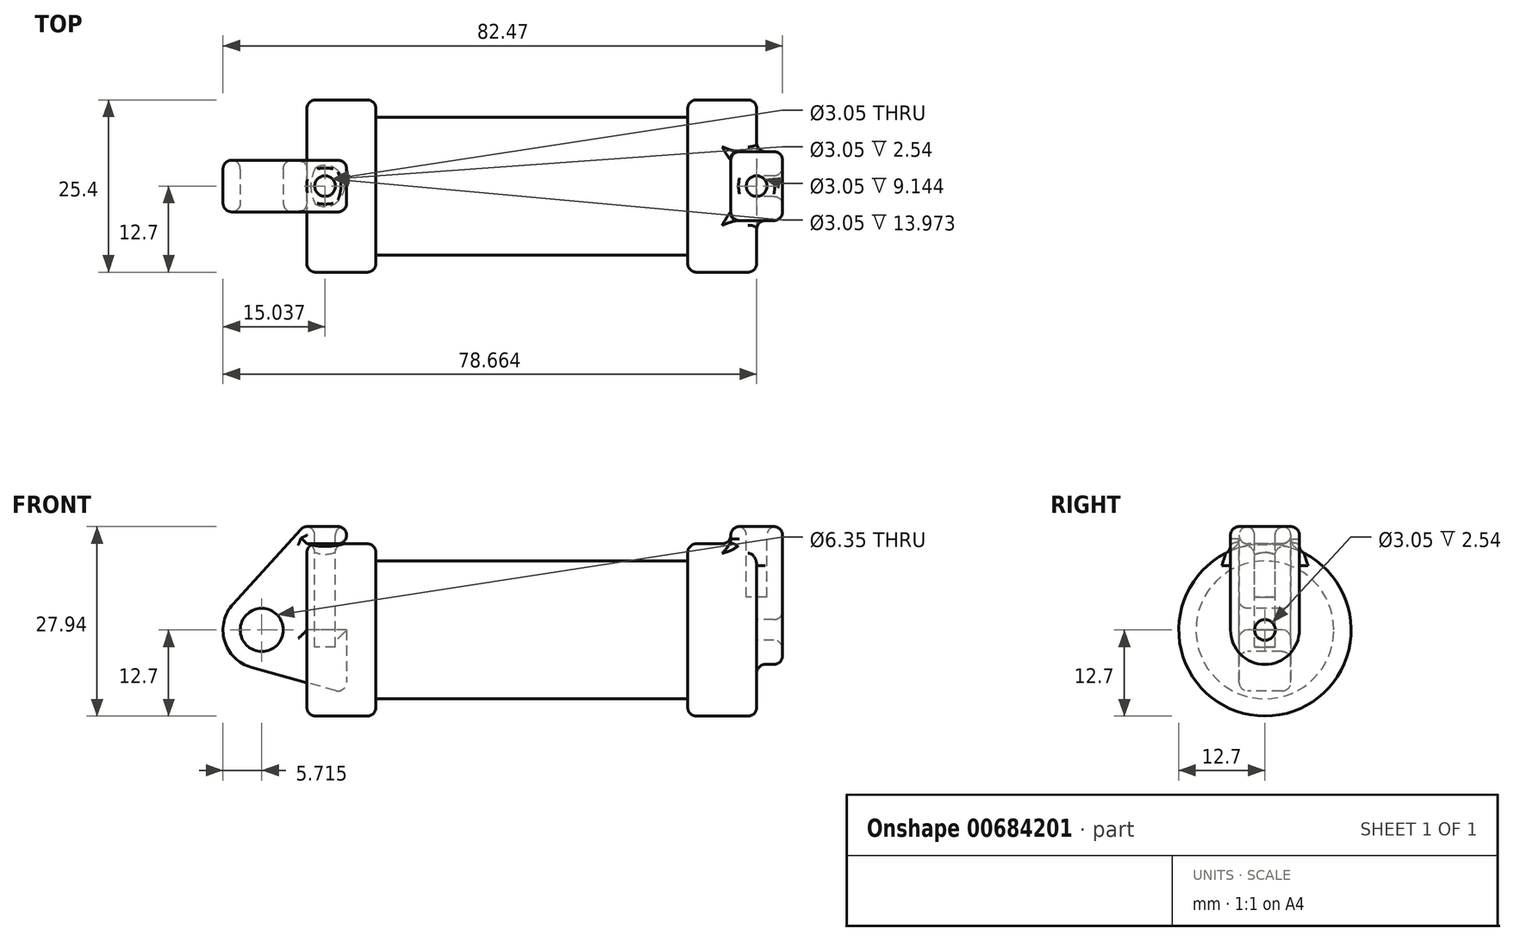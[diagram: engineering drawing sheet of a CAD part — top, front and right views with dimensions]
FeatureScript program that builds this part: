
annotation { "Feature Type Name" : "Feature", "Feature Type Description" : "" }
export const myFeature = defineFeature(function(context is Context, id is Id, definition is map)
    precondition{}
    {
        {
            var Q0;
            Q0=qCreatedBy(makeId("Front.planeOp"),FACE);
            var sketch = newSketch(context, id + "F0", { "sketchPlane" : qUnion([Q0])});
            skLineSegment(sketch, "E0", {"start": v(0, 0) * mm, "end": v(0, 12.7) * mm});
            skLineSegment(sketch, "E1", {"start": v(0, 12.7) * mm, "end": v(10.16, 12.7) * mm});
            skLineSegment(sketch, "E2", {"start": v(10.16, 12.7) * mm, "end": v(10.16, 10.16) * mm});
            skLineSegment(sketch, "E3", {"start": v(10.16, 10.16) * mm, "end": v(56.13, 10.16) * mm});
            skLineSegment(sketch, "E4", {"start": v(56.13, 10.16) * mm, "end": v(56.13, 12.7) * mm});
            skLineSegment(sketch, "E5", {"start": v(56.13, 12.7) * mm, "end": v(66.3, 12.7) * mm});
            skLineSegment(sketch, "E6", {"start": v(66.3, 12.7) * mm, "end": v(66.3, 0) * mm});
            skLineSegment(sketch, "E7", {"start": v(66.3, 0) * mm, "end": v(0, 0) * mm});
            skLineSegment(sketch, "E8", {"start": v(5.84, 15.24) * mm, "end": v(-0.5, 15.24) * mm});
            skLineSegment(sketch, "E9", {"start": v(-0.5, 15.24) * mm, "end": v(-10.88, 3.85) * mm});
            skLineSegment(sketch, "E10", {"start": v(0, 0) * mm, "end": v(-6.65, 0) * mm});
            skCircle(sketch, "E11", {"center": v(-6.65, 0) * mm, "radius": 5.72 * mm});
            skCircle(sketch, "E12", {"center": v(-6.65, 0) * mm, "radius": 3.18 * mm});
            skLineSegment(sketch, "E13", {"start": v(5.84, 15.24) * mm, "end": v(5.84, -9.4) * mm});
            skLineSegment(sketch, "E14", {"start": v(5.84, -9.4) * mm, "end": v(-8.18, -5.5) * mm});
            skSolve(sketch);
        }
        {
            var Q0;
            {var subQ0=sQuery(id+"F0.wireOp",EDGE,"E0");Q0=makeQuery(id+"F0.imprint","IMPRINT",FACE,{"disambiguationData":[TD([[makeQuery(id+"F0.imprint","IMPRINT",EDGE,{"derivedFrom":subQ0}),-1.0]])]});}
            var Q1;
            {var subQ0=sQuery(id+"F0.wireOp",EDGE,"E2");Q1=makeQuery(id+"F0.imprint","IMPRINT",FACE,{"disambiguationData":[TD([[makeQuery(id+"F0.imprint","IMPRINT",EDGE,{"derivedFrom":subQ0}),-1.0]])]});}
            var Q2;
            Q2=sQuery(id+"F0.wireOp",EDGE,"E7");
            var Q3;
            Q3=sQuery(id+"F0.wireOp",EDGE,"E7");
            revolve(context, id + "F1", {"entities" : qUnion([Q0, Q1]), "surfaceEntities" : qUnion([Q2]), "axis" : qUnion([Q3]), "revolveType" : RevolveType.FULL});
        }
        {
            var Q0;
            Q0=makeQuery(id+"F1.opRevolve","SWEPT_FACE",FACE,{"disambiguationData":[OSD([sQuery(id+"F0.wireOp",EDGE,"E6")])]});
            var sketch = newSketch(context, id + "F2", { "sketchPlane" : qUnion([Q0])});
            skCircle(sketch, "E15", {"center": v(0, 0) * mm, "radius": 5.08 * mm});
            skCircle(sketch, "E16", {"center": v(0, 0) * mm, "radius": 1.52 * mm});
            skPoint(sketch, "E17.start.orphan", {"position": v(12.7, 0) * mm});
            skLineSegment(sketch, "E18", {"start": v(-5.08, 0) * mm, "end": v(-5.08, 15.24) * mm});
            skLineSegment(sketch, "E19", {"start": v(5.08, 0) * mm, "end": v(5.08, 15.24) * mm});
            skLineSegment(sketch, "E20", {"start": v(-5.08, 15.24) * mm, "end": v(5.08, 15.24) * mm});
            skSolve(sketch);
        }
        {
            var Q0;
            {var subQ0=sQuery(id+"F0.wireOp",EDGE,"E14");Q0=makeQuery(id+"F0.imprint","IMPRINT",FACE,{"disambiguationData":[TD([[makeQuery(id+"F0.imprint","IMPRINT",EDGE,{"derivedFrom":subQ0}),-1.0]])]});}
            var Q1;
            {var subQ5=sQuery(id+"F0.wireOp",EDGE,"E12");Q1=makeQuery(id+"F0.imprint","IMPRINT",FACE,{"disambiguationData":[TD([[makeQuery(id+"F0.imprint","IMPRINT",EDGE,{"derivedFrom":subQ5}),-1.0]])]});}
            var Q2;
            {var subQ1=sQuery(id+"F0.wireOp",EDGE,"E0");Q2=makeQuery(id+"F0.imprint","IMPRINT",FACE,{"disambiguationData":[TD([[makeQuery(id+"F0.imprint","IMPRINT",EDGE,{"derivedFrom":subQ1}),1.0]])]});}
            extrude(context, id + "F3", {"entities" : qUnion([Q0, Q1, Q2]), "endBound" : BoundingType.SYMMETRIC, "oppositeDirection" : true, "depth" : 7.62 * mm, "offsetDistance" : 25.4 * mm});
        }
        {
            var Q0;
            Q0 = qSketchRegion(id + "F2", true);
            extrude(context, id + "F4", {"entities" : qUnion([Q0]), "operationType" : NewBodyOperationType.ADD, "endBound" : BoundingType.SYMMETRIC, "depth" : 7.62 * mm, "offsetDistance" : 25.4 * mm});
        }
        {
            var Q0;
            Q0=makeQuery(id+"F3.opExtrude","SWEPT_FACE",FACE,{"disambiguationData":[OSD([sQuery(id+"F0.wireOp",EDGE,"E8")])]});
            var sketch = newSketch(context, id + "F5", { "sketchPlane" : qUnion([Q0])});
            skCircle(sketch, "E21", {"center": v(2.67, 0) * mm, "radius": 1.52 * mm});
            skPoint(sketch, "E21.centerSnap0", {"position": v(-0.5, 0) * mm});
            skPoint(sketch, "E21.centerSnap1", {"position": v(2.67, -3.81) * mm});
            skSolve(sketch);
        }
        {
            var Q0;
            Q0=makeQuery(id+"F4.opExtrude","SWEPT_FACE",FACE,{"disambiguationData":[OSD([sQuery(id+"F2.wireOp",EDGE,"E20")])]});
            var sketch = newSketch(context, id + "F6", { "sketchPlane" : qUnion([Q0])});
            skCircle(sketch, "E22", {"center": v(66.3, 0) * mm, "radius": 1.52 * mm});
            skPoint(sketch, "E22.centerSnap0", {"position": v(66.3, -5.08) * mm});
            skPoint(sketch, "E22.centerSnap1", {"position": v(62.48, 0) * mm});
            skSolve(sketch);
        }
        {
            var Q0;
            Q0 = qSketchRegion(id + "F6", true);
            extrude(context, id + "F7", {"entities" : qUnion([Q0]), "operationType" : NewBodyOperationType.REMOVE, "oppositeDirection" : true, "depth" : 10.4 * mm, "offsetDistance" : 25.4 * mm});
        }
        {
            var Q0;
            Q0=makeQuery(id+"F5.imprint","IMPRINT",FACE,{"disambiguationData":[TD([[makeQuery(id+"F5.imprint","IMPRINT",EDGE,{"derivedFrom":sQuery(id+"F5.wireOp",EDGE,"E21")}),1.0]])]});
            extrude(context, id + "F8", {"entities" : qUnion([Q0]), "operationType" : NewBodyOperationType.REMOVE, "oppositeDirection" : true, "depth" : 17.78 * mm, "offsetDistance" : 25.4 * mm});
        }
        {
            var Q0;
            Q0=makeQuery(id+"F1.opRevolve","SWEPT_FACE",FACE,{"disambiguationData":[OSD([sQuery(id+"F0.wireOp",EDGE,"E5")])]});
            var Q1;
            Q1=makeQuery(id+"F1.opRevolve","SWEPT_FACE",FACE,{"disambiguationData":[OSD([sQuery(id+"F0.wireOp",EDGE,"E1")])]});
            fillet(context, id + "F9", {"entities" : qUnion([Q0, Q1]), "radius" : 1.27 * mm, "tangentPropagation" : true, "allowEdgeOverflow" : false});
        }
        {
            var Q0;
            Q0=makeQuery(id+"F3.opExtrude","CAP_FACE",FACE,{"disambiguationData":[OSD([sQuery(id+"F0.wireOp",EDGE,"E0"),sQuery(id+"F0.wireOp",EDGE,"E1"),sQuery(id+"F0.wireOp",EDGE,"E7"),sQuery(id+"F0.wireOp",EDGE,"E8"),sQuery(id+"F0.wireOp",EDGE,"E9"),sQuery(id+"F0.wireOp",EDGE,"E11"),sQuery(id+"F0.wireOp",EDGE,"E12"),sQuery(id+"F0.wireOp",EDGE,"E13"),sQuery(id+"F0.wireOp",EDGE,"E14")])],"isStart":false});
            var Q1;
            Q1=makeQuery(id+"F3.opExtrude","CAP_FACE",FACE,{"disambiguationData":[OSD([sQuery(id+"F0.wireOp",EDGE,"E0"),sQuery(id+"F0.wireOp",EDGE,"E1"),sQuery(id+"F0.wireOp",EDGE,"E7"),sQuery(id+"F0.wireOp",EDGE,"E8"),sQuery(id+"F0.wireOp",EDGE,"E9"),sQuery(id+"F0.wireOp",EDGE,"E11"),sQuery(id+"F0.wireOp",EDGE,"E12"),sQuery(id+"F0.wireOp",EDGE,"E13"),sQuery(id+"F0.wireOp",EDGE,"E14")])],"isStart":true});
            var Q2;
            Q2=makeQuery(id+"F3.opExtrude","SWEPT_FACE",FACE,{"disambiguationData":[OSD([sQuery(id+"F0.wireOp",EDGE,"E9")])]});
            var Q3;
            Q3=makeQuery(id+"F3.opExtrude","SWEPT_FACE",FACE,{"disambiguationData":[OSD([sQuery(id+"F0.wireOp",EDGE,"E11")])]});
            var Q4;
            Q4=makeQuery(id+"F3.opExtrude","SWEPT_FACE",FACE,{"disambiguationData":[OSD([sQuery(id+"F0.wireOp",EDGE,"E14")])]});
            var Q5;
            Q5=makeQuery(id+"F3.opExtrude","SWEPT_FACE",FACE,{"disambiguationData":[OSD([sQuery(id+"F0.wireOp",EDGE,"E8")])]});
            var Q6;
            {var subQ0=sQuery(id+"F0.wireOp",EDGE,"E13");Q6=makeQuery(id+"F3.opExtrude","SWEPT_FACE",FACE,{"disambiguationData":[OSD([subQ0]),TDD([makeQuery(id+"F0.imprint","IMPRINT",EDGE,{"disambiguationData":[TD([[makeQuery(id+"F0.imprint","INTERSECT",VERTEX,{"derivedFrom":[sQuery(id+"F0.wireOp",EDGE,"E8"),subQ0]}),-1.0]])],"derivedFrom":subQ0})])]});}
            fillet(context, id + "F10", {"entities" : qUnion([Q0, Q1, Q2, Q3, Q4, Q5, Q6]), "radius" : 1.27 * mm, "tangentPropagation" : true, "allowEdgeOverflow" : false});
        }
        {
            var Q0;
            Q0=makeQuery(id+"F4.opExtrude","CAP_FACE",FACE,{"disambiguationData":[OSD([sQuery(id+"F2.wireOp",EDGE,"E15"),sQuery(id+"F2.wireOp",EDGE,"E16"),sQuery(id+"F2.wireOp",EDGE,"E18"),sQuery(id+"F2.wireOp",EDGE,"E19"),sQuery(id+"F2.wireOp",EDGE,"E20")])],"isStart":false});
            var Q1;
            Q1=makeQuery(id+"F4.opExtrude","SWEPT_FACE",FACE,{"disambiguationData":[OSD([sQuery(id+"F2.wireOp",EDGE,"E20")])]});
            var Q2;
            Q2=makeQuery(id+"F4.opExtrude","SWEPT_FACE",FACE,{"disambiguationData":[OSD([sQuery(id+"F2.wireOp",EDGE,"E18")])]});
            var Q3;
            Q3=makeQuery(id+"F4.opExtrude","SWEPT_FACE",FACE,{"disambiguationData":[OSD([sQuery(id+"F2.wireOp",EDGE,"E19")])]});
            var Q4;
            Q4=makeQuery(id+"F4.opExtrude","SWEPT_FACE",FACE,{"disambiguationData":[OSD([sQuery(id+"F2.wireOp",EDGE,"E15")])]});
            var Q5;
            Q5=makeQuery(id+"F4.opExtrude","CAP_FACE",FACE,{"disambiguationData":[OSD([sQuery(id+"F2.wireOp",EDGE,"E15"),sQuery(id+"F2.wireOp",EDGE,"E16"),sQuery(id+"F2.wireOp",EDGE,"E18"),sQuery(id+"F2.wireOp",EDGE,"E19"),sQuery(id+"F2.wireOp",EDGE,"E20")])],"isStart":true});
            fillet(context, id + "F11", {"entities" : qUnion([Q0, Q1, Q2, Q3, Q4, Q5]), "radius" : 1.27 * mm, "tangentPropagation" : true, "allowEdgeOverflow" : false});
        }
    });
